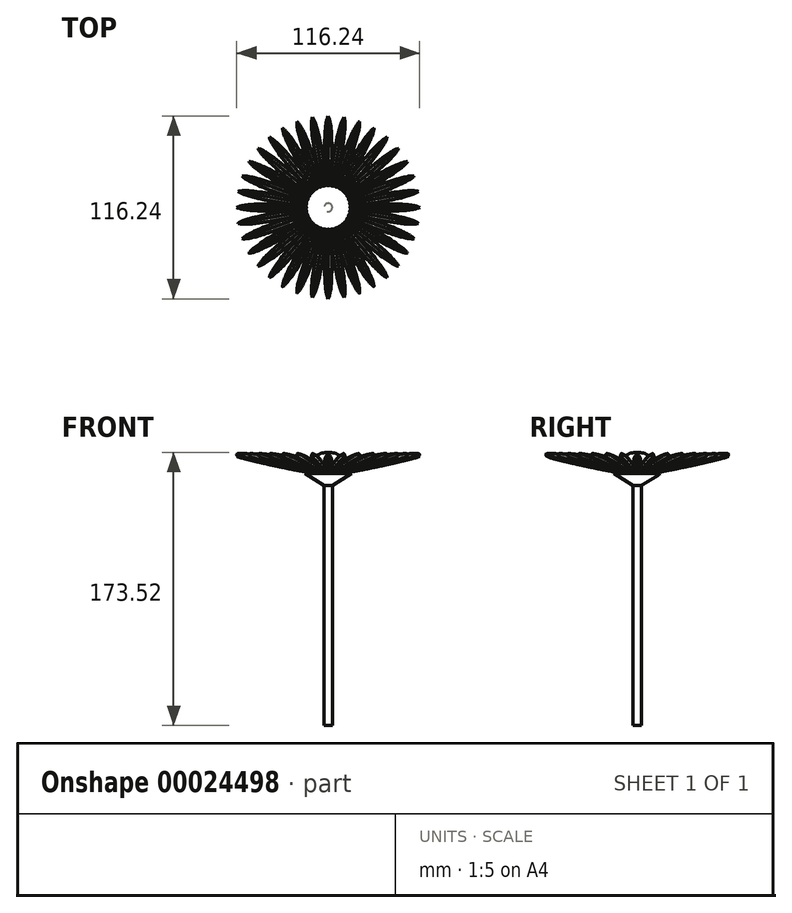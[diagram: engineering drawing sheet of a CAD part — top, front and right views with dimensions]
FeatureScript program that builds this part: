
annotation { "Feature Type Name" : "Feature", "Feature Type Description" : "" }
export const myFeature = defineFeature(function(context is Context, id is Id, definition is map)
    precondition{}
    {
        {
            var Q0;
            Q0=qCreatedBy(makeId("Front.planeOp"),FACE);
            var sketch = newSketch(context, id + "F0", { "sketchPlane" : qUnion([Q0])});
            skArc(sketch, "E0", {"start": v(0, 0) * mm, "mid": v(-33.58, 11.48) * mm, "end": v(-68.88, 15.09) * mm});
            skArc(sketch, "E1", {"start": v(-68.88, 15.09) * mm, "mid": v(-34.69, 6.43) * mm, "end": v(0, 0) * mm});
            skSolve(sketch);
        }
        {
            var Q0;
            Q0 = qSketchRegion(id + "F0", true);
            extrude(context, id + "F1", {"entities" : qUnion([Q0]), "depth" : 2.54 * mm, "hasSecondDirection" : true, "secondDirectionOppositeDirection" : true, "secondDirectionDepth" : 2.54 * mm});
        }
        {
            var Q0;
            Q0=qCreatedBy(makeId("Top.planeOp"),FACE);
            var sketch = newSketch(context, id + "F2", { "sketchPlane" : qUnion([Q0])});
            skArc(sketch, "E2", {"start": v(-65.64, 2.57) * mm, "mid": v(-67.67, 1.74) * mm, "end": v(-69.02, 0) * mm});
            skLineSegment(sketch, "E3", {"start": v(-70.6, 0) * mm, "end": v(-69.02, 0) * mm});
            skLineSegment(sketch, "E4", {"start": v(-65.64, 2.57) * mm, "end": v(-65.6, 4.72) * mm});
            skFitSpline(sketch, "E5", {"points": [v(-70.6, 0) * mm, v(-68.66, 3.9) * mm, v(-65.6, 4.72) * mm], "startDerivative": vector(2.76, 8.72) * mm, "endDerivative": vector(7.36, 0.5) * mm});
            skSolve(sketch);
        }
        {
            var Q0;
            Q0=makeQuery(id+"F2.imprint","IMPRINT",FACE,{"disambiguationData":[TD([[makeQuery(id+"F2.imprint","IMPRINT",EDGE,{"derivedFrom":sQuery(id+"F2.wireOp",EDGE,"E2")}),1.0]])]});
            var Q1;
            Q1=makeQuery(id+"F2.imprint","IMPRINT",FACE,{"disambiguationData":[TD([[makeQuery(id+"F2.imprint","IMPRINT",EDGE,{"derivedFrom":sQuery(id+"F2.wireOp",EDGE,"E2")}),-1.0]])]});
            extrude(context, id + "F3", {"entities" : qUnion([Q0, Q1]), "operationType" : NewBodyOperationType.REMOVE, "depth" : 304.8 * mm});
        }
        {
            var Q0;
            Q0=qCreatedBy(makeId("Top.planeOp"),FACE);
            var sketch = newSketch(context, id + "F4", { "sketchPlane" : qUnion([Q0])});
            skLineSegment(sketch, "E6", {"start": v(-72.27, 0) * mm, "end": v(-55.26, 0) * mm});
            skLineSegment(sketch, "E7", {"start": v(-55.26, 0) * mm, "end": v(5.2, 0) * mm});
            skLineSegment(sketch, "E8", {"start": v(5.2, 0) * mm, "end": v(1.96, -22.3) * mm});
            skLineSegment(sketch, "E9", {"start": v(-72.27, 0) * mm, "end": v(-72.27, -19.55) * mm});
            skLineSegment(sketch, "E10", {"start": v(1.96, -22.3) * mm, "end": v(-60.83, -17.6) * mm});
            skLineSegment(sketch, "E11", {"start": v(-72.27, -19.55) * mm, "end": v(-60.83, -17.6) * mm});
            skSolve(sketch);
        }
        {
            var Q0;
            Q0 = qSketchRegion(id + "F4", true);
            extrude(context, id + "F5", {"entities" : qUnion([Q0]), "operationType" : NewBodyOperationType.REMOVE, "depth" : 304.8 * mm});
        }
        {
            var Q0;
            Q0=makeQuery(id+"F1.opExtrude","SWEPT_BODY",BODY,{"disambiguationData":[OSD([sQuery(id+"F0.wireOp",EDGE,"E0"),sQuery(id+"F0.wireOp",EDGE,"E1")])]});
            var Q1;
            Q1=makeQuery(id+"F5.boolean.opBoolean","COPY",FACE,{"derivedFrom":makeQuery(id+"F5.opExtrude","SWEPT_FACE",FACE,{"disambiguationData":[OSD([sQuery(id+"F4.wireOp",EDGE,"E6"),sQuery(id+"F4.wireOp",EDGE,"E7")])]})});
            mirror(context, id + "F6", {"operationType" : NewBodyOperationType.ADD, "entities" : qUnion([Q0]), "mirrorPlane" : qUnion([Q1])});
        }
        {
            var Q0;
            Q0=makeQuery(id+"F6.opPattern","COPY",EDGE,{"derivedFrom":makeQuery(id+"F1.opExtrude","CAP_EDGE",EDGE,{"disambiguationData":[OSD([sQuery(id+"F0.wireOp",EDGE,"E0")])],"isStart":true}),"instanceName":"1"});
            var Q1;
            Q1=makeQuery(id+"F1.opExtrude","CAP_EDGE",EDGE,{"disambiguationData":[OSD([sQuery(id+"F0.wireOp",EDGE,"E0")])],"isStart":true});
            fillet(context, id + "F7", {"entities" : qUnion([Q0, Q1]), "radius" : 5.08 * mm, "tangentPropagation" : true, "allowEdgeOverflow" : false});
        }
        {
            var Q0;
            Q0=makeQuery(id+"F6.opPattern","COPY",EDGE,{"derivedFrom":makeQuery(id+"F1.opExtrude","CAP_EDGE",EDGE,{"disambiguationData":[OSD([sQuery(id+"F0.wireOp",EDGE,"E1")])],"isStart":true}),"instanceName":"1"});
            var Q1;
            Q1=makeQuery(id+"F1.opExtrude","CAP_EDGE",EDGE,{"disambiguationData":[OSD([sQuery(id+"F0.wireOp",EDGE,"E1")])],"isStart":true});
            var Q2;
            {var subQ0=makeQuery(id+"F1.opExtrude","SWEPT_FACE",FACE,{"disambiguationData":[OSD([sQuery(id+"F0.wireOp",EDGE,"E1")])]});Q2=makeQuery(id+"F7.opFillet","BLEND_EDGE",EDGE,{"disambiguationData":[OD(1.0)],"blendedFrom":[makeQuery(id+"F6.opPattern","COPY",EDGE,{"derivedFrom":makeQuery(id+"F1.opExtrude","CAP_EDGE",EDGE,{"disambiguationData":[OSD([sQuery(id+"F0.wireOp",EDGE,"E0")])],"isStart":true}),"instanceName":"1"}),makeQuery(id+"F6.boolean.opBoolean","MERGE",FACE,{"derivedFrom":[subQ0,makeQuery(id+"F6.opPattern","COPY",FACE,{"derivedFrom":subQ0,"instanceName":"1"})]})],"blendedInto":[makeQuery(id+"F6.boolean.opBoolean","MERGE",FACE,{"derivedFrom":[subQ0,makeQuery(id+"F6.opPattern","COPY",FACE,{"derivedFrom":subQ0,"instanceName":"1"})]})]});}
            var Q3;
            {var subQ0=makeQuery(id+"F1.opExtrude","SWEPT_FACE",FACE,{"disambiguationData":[OSD([sQuery(id+"F0.wireOp",EDGE,"E1")])]});Q3=makeQuery(id+"F7.opFillet","BLEND_EDGE",EDGE,{"disambiguationData":[OD(0.0)],"blendedFrom":[makeQuery(id+"F6.opPattern","COPY",EDGE,{"derivedFrom":makeQuery(id+"F1.opExtrude","CAP_EDGE",EDGE,{"disambiguationData":[OSD([sQuery(id+"F0.wireOp",EDGE,"E0")])],"isStart":true}),"instanceName":"1"}),makeQuery(id+"F6.boolean.opBoolean","MERGE",FACE,{"derivedFrom":[subQ0,makeQuery(id+"F6.opPattern","COPY",FACE,{"derivedFrom":subQ0,"instanceName":"1"})]})],"blendedInto":[makeQuery(id+"F6.boolean.opBoolean","MERGE",FACE,{"derivedFrom":[subQ0,makeQuery(id+"F6.opPattern","COPY",FACE,{"derivedFrom":subQ0,"instanceName":"1"})]})]});}
            var Q4;
            {var subQ0=makeQuery(id+"F1.opExtrude","SWEPT_FACE",FACE,{"disambiguationData":[OSD([sQuery(id+"F0.wireOp",EDGE,"E1")])]});Q4=makeQuery(id+"F7.opFillet","BLEND_EDGE",EDGE,{"disambiguationData":[OD(0.0)],"blendedFrom":[makeQuery(id+"F1.opExtrude","CAP_EDGE",EDGE,{"disambiguationData":[OSD([sQuery(id+"F0.wireOp",EDGE,"E0")])],"isStart":true}),makeQuery(id+"F6.boolean.opBoolean","MERGE",FACE,{"derivedFrom":[subQ0,makeQuery(id+"F6.opPattern","COPY",FACE,{"derivedFrom":subQ0,"instanceName":"1"})]})],"blendedInto":[makeQuery(id+"F6.boolean.opBoolean","MERGE",FACE,{"derivedFrom":[subQ0,makeQuery(id+"F6.opPattern","COPY",FACE,{"derivedFrom":subQ0,"instanceName":"1"})]})]});}
            var Q5;
            {var subQ0=makeQuery(id+"F1.opExtrude","SWEPT_FACE",FACE,{"disambiguationData":[OSD([sQuery(id+"F0.wireOp",EDGE,"E1")])]});Q5=makeQuery(id+"F7.opFillet","BLEND_EDGE",EDGE,{"disambiguationData":[OD(1.0)],"blendedFrom":[makeQuery(id+"F1.opExtrude","CAP_EDGE",EDGE,{"disambiguationData":[OSD([sQuery(id+"F0.wireOp",EDGE,"E0")])],"isStart":true}),makeQuery(id+"F6.boolean.opBoolean","MERGE",FACE,{"derivedFrom":[subQ0,makeQuery(id+"F6.opPattern","COPY",FACE,{"derivedFrom":subQ0,"instanceName":"1"})]})],"blendedInto":[makeQuery(id+"F6.boolean.opBoolean","MERGE",FACE,{"derivedFrom":[subQ0,makeQuery(id+"F6.opPattern","COPY",FACE,{"derivedFrom":subQ0,"instanceName":"1"})]})]});}
            fillet(context, id + "F8", {"entities" : qUnion([Q0, Q1, Q2, Q3, Q4, Q5]), "radius" : 1.27 * mm, "tangentPropagation" : true, "allowEdgeOverflow" : false});
        }
        {
            var Q0;
            Q0=qCreatedBy(makeId("Top.planeOp"),FACE);
            var sketch = newSketch(context, id + "F9", { "sketchPlane" : qUnion([Q0])});
            skCircle(sketch, "E12", {"center": v(0, 0) * mm, "radius": 6.94 * mm});
            skSolve(sketch);
        }
        {
            var Q0;
            Q0=makeQuery(id+"F1.opExtrude","SWEPT_BODY",BODY,{"disambiguationData":[OSD([sQuery(id+"F0.wireOp",EDGE,"E0"),sQuery(id+"F0.wireOp",EDGE,"E1")])]});
            var Q1;
            Q1=sQuery(id+"F9.wireOp",EDGE,"E12");
            circularPattern(context, id + "F10", {"operationType" : NewBodyOperationType.ADD, "entities" : qUnion([Q0]), "axis" : qUnion([Q1]), "angle" : 10 * degree, "instanceCount" : 36});
        }
        {
            var Q0;
            Q0=qCreatedBy(makeId("Top.planeOp"),FACE);
            var sketch = newSketch(context, id + "F11", { "sketchPlane" : qUnion([Q0])});
            skCircle(sketch, "E13", {"center": v(0, 0) * mm, "radius": 14.77 * mm});
            skLineSegment(sketch, "E14", {"start": v(-14.77, 0) * mm, "end": v(14.77, 0) * mm});
            skSolve(sketch);
        }
        {
            var Q0;
            {var subQ0=sQuery(id+"F11.wireOp",EDGE,"E14");Q0=makeQuery(id+"F11.imprint","IMPRINT",FACE,{"disambiguationData":[TD([[makeQuery(id+"F11.imprint","IMPRINT",EDGE,{"derivedFrom":subQ0}),1.0]])]});}
            var Q1;
            Q1=sQuery(id+"F11.wireOp",EDGE,"E14");
            revolve(context, id + "F12", {"operationType" : NewBodyOperationType.ADD, "entities" : qUnion([Q0]), "axis" : qUnion([Q1]), "revolveType" : RevolveType.ONE_DIRECTION, "angle" : 180 * degree});
        }
        {
            var Q0;
            Q0=makeQuery(id+"F12.opRevolve","CAP_FACE",FACE,{"disambiguationData":[OSD([sQuery(id+"F11.wireOp",EDGE,"E13"),sQuery(id+"F11.wireOp",EDGE,"E14")])],"isStart":true});
            var sketch = newSketch(context, id + "F13", { "sketchPlane" : qUnion([Q0])});
            skCircle(sketch, "E15", {"center": v(0, 0) * mm, "radius": 16.96 * mm});
            skSolve(sketch);
        }
        {
            var Q0;
            Q0 = qSketchRegion(id + "F13", true);
            extrude(context, id + "F14", {"entities" : qUnion([Q0]), "operationType" : NewBodyOperationType.REMOVE, "oppositeDirection" : true, "depth" : 1.27 * mm, "hasSecondDirection" : true, "secondDirectionOppositeDirection" : false, "secondDirectionDepth" : 25.4 * mm});
        }
        {
            var Q0;
            Q0=makeQuery(id+"F14.boolean.opBoolean","COPY",FACE,{"derivedFrom":makeQuery(id+"F14.opExtrude","CAP_FACE",FACE,{"disambiguationData":[OSD([sQuery(id+"F13.wireOp",EDGE,"E15")])],"isStart":false})});
            cPlane(context, id + "F15", {"entities" : qUnion([Q0]), "cplaneType" : CPlaneType.OFFSET, "offset" : 7.62 * mm, "width" : 152.4 * mm, "height" : 152.4 * mm});
        }
        {
            var Q0;
            Q0=qCreatedBy(id+"F15.planeOp",FACE);
            var sketch = newSketch(context, id + "F16", { "sketchPlane" : qUnion([Q0])});
            skCircle(sketch, "E16", {"center": v(0, 0) * mm, "radius": 2.62 * mm});
            skSolve(sketch);
        }
        {
            var Q1;
            Q1=makeQuery(id+"F14.boolean.opBoolean","COPY",FACE,{"derivedFrom":makeQuery(id+"F14.opExtrude","CAP_FACE",FACE,{"disambiguationData":[OSD([sQuery(id+"F13.wireOp",EDGE,"E15")])],"isStart":false})});
            var Q2;
            Q2=makeQuery(id+"F16.imprint","IMPRINT",FACE,{"disambiguationData":[TD([[makeQuery(id+"F16.imprint","IMPRINT",EDGE,{"derivedFrom":sQuery(id+"F16.wireOp",EDGE,"E16")}),1.0]])]});
            loft(context, id + "F17", {"sheetProfilesArray" : [{ "sheetProfileEntities" : qUnion([Q1]) }, { "sheetProfileEntities" : qUnion([Q2]) }]});
        }
        {
            var Q0;
            Q0=makeQuery(id+"F17.opLoft","CAP_FACE",FACE,{"disambiguationData":[OSD([makeQuery(id+"F16.imprint","IMPRINT",FACE,{"disambiguationData":[TD([[makeQuery(id+"F16.imprint","IMPRINT",EDGE,{"derivedFrom":sQuery(id+"F16.wireOp",EDGE,"E16")}),1.0]])]})])],"isStart":true});
            extrude(context, id + "F18", {"entities" : qUnion([Q0]), "operationType" : NewBodyOperationType.ADD, "depth" : 152.4 * mm});
        }
    });
